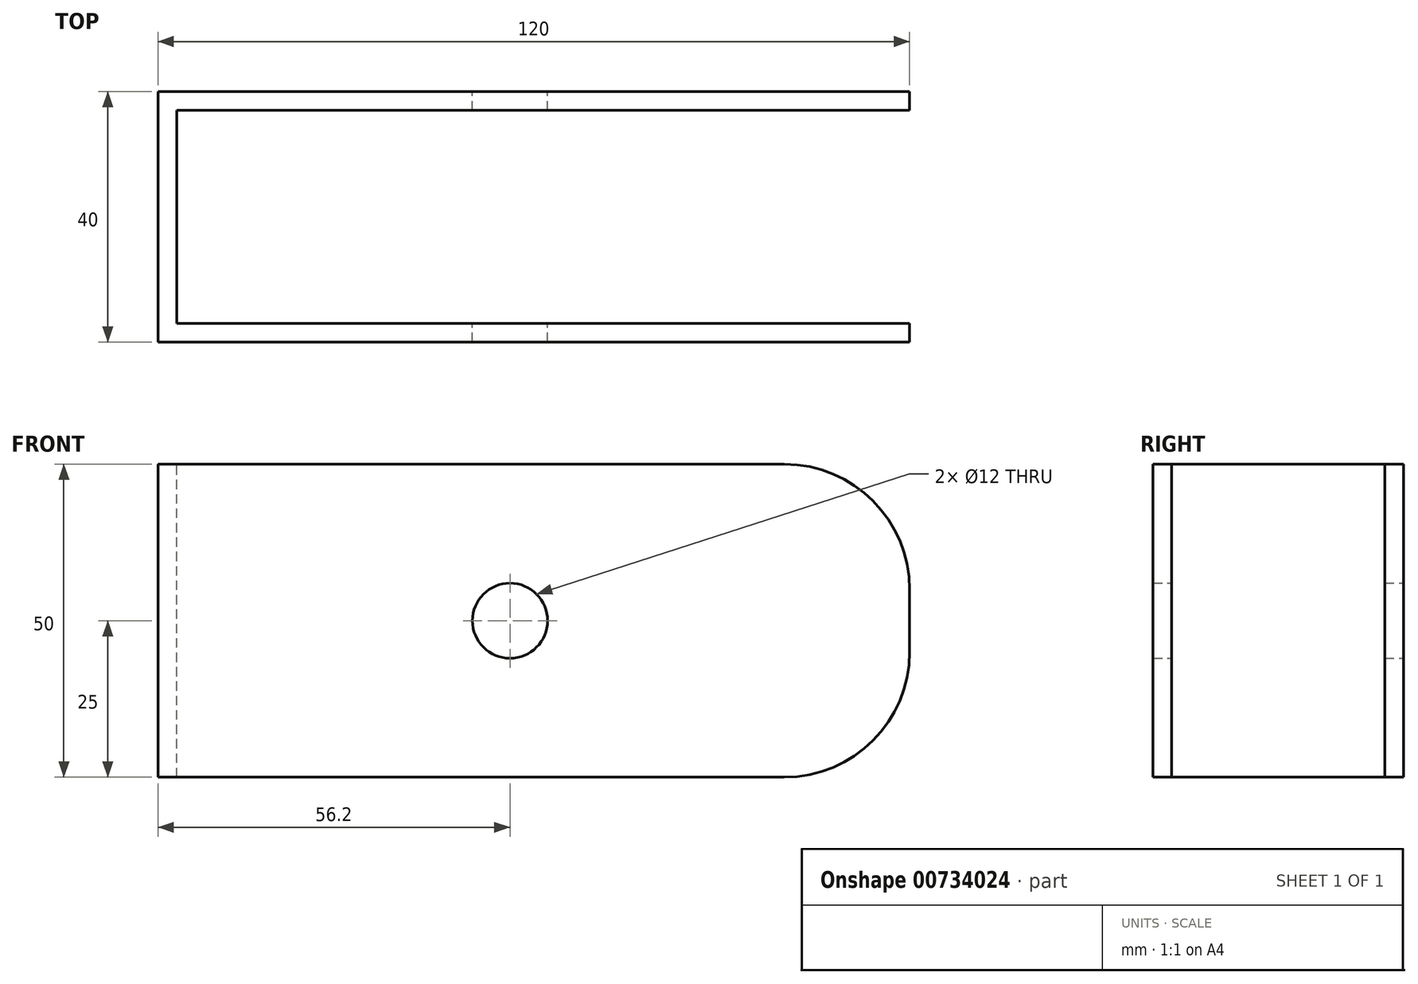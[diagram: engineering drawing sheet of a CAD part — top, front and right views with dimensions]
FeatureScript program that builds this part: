
annotation { "Feature Type Name" : "Feature", "Feature Type Description" : "" }
export const myFeature = defineFeature(function(context is Context, id is Id, definition is map)
    precondition{}
    {
        {
            var Q0;
            Q0=qCreatedBy(makeId("Front.planeOp"),FACE);
            var sketch = newSketch(context, id + "F0", { "sketchPlane" : qUnion([Q0])});
            skLineSegment(sketch, "E0", {"start": v(-60, 25) * mm, "end": v(-60, -25) * mm});
            skLineSegment(sketch, "E1", {"start": v(-60, -25) * mm, "end": v(40, -25) * mm});
            skLineSegment(sketch, "E2", {"start": v(60, -5) * mm, "end": v(60, 5) * mm});
            skLineSegment(sketch, "E3", {"start": v(40, 25) * mm, "end": v(-60, 25) * mm});
            skPoint(sketch, "E4.visualSharp", {"position": v(60, 25) * mm});
            skArc(sketch, "E4.filletArc", {"start": v(60, 5) * mm, "mid": v(54.14, 19.14) * mm, "end": v(40, 25) * mm});
            skPoint(sketch, "E5.visualSharp", {"position": v(60, -25) * mm});
            skArc(sketch, "E5.filletArc", {"start": v(40, -25) * mm, "mid": v(54.14, -19.14) * mm, "end": v(60, -5) * mm});
            skSolve(sketch);
        }
        {
            var Q0;
            Q0=makeQuery(id+"F0.imprint","IMPRINT",FACE,{"disambiguationData":[TD([[makeQuery(id+"F0.imprint","IMPRINT",EDGE,{"derivedFrom":sQuery(id+"F0.wireOp",EDGE,"E0")}),1.0]])]});
            extrude(context, id + "F1", {"entities" : qUnion([Q0]), "endBound" : BoundingType.SYMMETRIC, "depth" : 40 * mm, "offsetDistance" : 25 * mm});
        }
        {
            var Q0;
            Q0=makeQuery(id+"F1.opExtrude","SWEPT_FACE",FACE,{"disambiguationData":[OSD([sQuery(id+"F0.wireOp",EDGE,"E3")])]});
            var sketch = newSketch(context, id + "F2", { "sketchPlane" : qUnion([Q0])});
            skLineSegment(sketch, "E6.bottom", {"start": v(-57, 17) * mm, "end": v(83, 17) * mm});
            skLineSegment(sketch, "E6.top", {"start": v(-57, -17) * mm, "end": v(83, -17) * mm});
            skLineSegment(sketch, "E6.left", {"start": v(-57, 17) * mm, "end": v(-57, -17) * mm});
            skLineSegment(sketch, "E6.right", {"start": v(83, 17) * mm, "end": v(83, -17) * mm});
            skSolve(sketch);
        }
        {
            var Q0;
            Q0 = qSketchRegion(id + "F2", true);
            extrude(context, id + "F3", {"entities" : qUnion([Q0]), "operationType" : NewBodyOperationType.REMOVE, "oppositeDirection" : true, "depth" : 60 * mm, "offsetDistance" : 25 * mm});
        }
        {
            var Q0;
            Q0=makeQuery(id+"F1.opExtrude","CAP_FACE",FACE,{"disambiguationData":[OSD([sQuery(id+"F0.wireOp",EDGE,"E0"),sQuery(id+"F0.wireOp",EDGE,"E1"),sQuery(id+"F0.wireOp",EDGE,"E2"),sQuery(id+"F0.wireOp",EDGE,"E3"),sQuery(id+"F0.wireOp",EDGE,"E4.filletArc"),sQuery(id+"F0.wireOp",EDGE,"E5.filletArc")])],"isStart":true});
            var sketch = newSketch(context, id + "F4", { "sketchPlane" : qUnion([Q0])});
            skCircle(sketch, "E7", {"center": v(3.8, 0) * mm, "radius": 6 * mm});
            skSolve(sketch);
        }
        {
            var Q0;
            Q0 = qSketchRegion(id + "F4", true);
            extrude(context, id + "F5", {"entities" : qUnion([Q0]), "operationType" : NewBodyOperationType.REMOVE, "oppositeDirection" : true, "depth" : 50 * mm, "offsetDistance" : 25 * mm});
        }
    });
